# Revit family: Water_Heaters_HAJDU_HAJDU-CUBE_
name_source: partatom
category: Mechanical Equipment
units: mm (PartAtom-declared; Revit-internal decimal feet)

## family parameters
Classification = None
Cut with Voids When Loaded = No
Host = Face
Maintain Annotation Orientation = No
OmniClass Number = 23.31.29.13
OmniClass Title = Hot Water Tank Heaters
Part Type = Normal
Room Calculation Point = No
Round Connector Dimension = Use Diameter
Shared = No

## types (1)
- Nem típus - Terheléstípus katalógus!
    A melegvíz maximális homérséklete = 75 °C
    Csapolási profil = M
    Csatlakozás leírása = Elektromos csatlakozó
    Csatlakozó eltolás = 145 mm
    Default Elevation = 1219 mm
    Description = Az elektromos, zártrendszerű forróvíztárolók a használati melegvíz igény kielégítésére szolgálnak. A zártrendszerű tárolós vízmelegítők tartálya acéllemezből készül, a korrózió elleni védelmet speciális, titán tartalmú tűzzománc bevonat és aktív magnézium anód biztosítja. Ezek a készülékek több vízvételi hely, illetve zuhanyzós csaptelepek ellátására alkalmasak. A készülékek hőszigetelése freonmentes, poliuretán szigetelő hab. A fémburkolatú kivitelek nanokerámiás felület előkészítéssel rendelkeznek.Az új generációs CUBE nevű sorozat készülékei Smart Control vezérlésű öntanuló rendszerrel rendelkeznek, melyek segítségével még hatékonyabban és energiatakarékosabban állíthatunk elő használati melegvizet.Kerámia (szteatitos) fűtőtesttel rendelkezik, aminek nagy előnye a csekély vízkőképződés, a hosszabb éltettartam, és a lényegesen kisebb szervizelési költség.
    Dimenzió "b" = 367 mm  [stored 1.20407 ft]
    Dimenzió "c" = 0 mm  [stored 0 ft]
    Dimenzió "e" = 300 mm
    Dimenzió "f" = 100 mm  [stored 0.328084 ft]
    Dimenzió "k" = 100 mm  [stored 0.328084 ft]
    Elhelyezés = Fali függőleges
    Energiahatékonysági osztály = B
    Felfutési ido 15°C-ról 65°C-ra = 2.63 h
    Feszültség = 230 V
    Frekvencia = 50 Hz
    Futobetét típusa = Kerámia
    Futoteljesítmény = 1200 W
    Fázisok száma = 1
    Házház anyaga = Hajdu - Felület - Fehér
    Látszólagos terhelés = 1380 VA
    Magasság = 587 mm  [stored 1.92585 ft]
    Manufacturer = HAJDU
    Model = Modell nincs megadva - Terheléstípus katalógus!
    Mélység = 490 mm  [stored 1.60761 ft]
    Névleges urtartalom = 50 l
    Névleges üzemi nyomás = 0.6 MPa
    Product Page URL = https://hajdurt.hu
    Rendeltetés = Zártrendszerű szögletes forróvíztároló
    Szélesség = 490 mm  [stored 1.60761 ft]
    Teljesítménytényezo = 1
    Tömeg = 50.00 kg
    URL = https://hajdurt.hu
    Védettségi fokozat = IPX4
    Vízcsatlakozás = 13 mm  [stored 0.0426509 ft]
    Áramfelvétel = 6 A
    Érintésvédelmi osztály = I.

note: [stored X ft] marks values corroborated as IEEE doubles in the binary element streams (Revit-internal decimal feet)

## geometry (parser evidence)
native form markers: Sweep x7
no freeform markers — native parametric forms only
